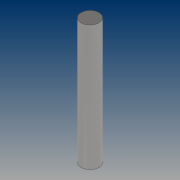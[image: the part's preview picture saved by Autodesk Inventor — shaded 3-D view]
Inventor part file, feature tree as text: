
AUTODESK INVENTOR PART (.ipt)
format: ipt  version: 2021 (Build 250183000, 183)  size: 74,752 bytes
history: native  units: mm
features: extrude x1, sketch x1
ambient origin geometry x8: Origin, YZ Plane, XZ Plane, XY Plane, X Axis, Y Axis, Z Axis, Center Point
bodies: Solid1 (feature_tree)
feature tree (2):
  extrude  "Extrusion1"  Depth=70.0mm TaperAngle=0.0deg
  sketch  "Sketch1"  dims[d0=10.0mm d1=70.0mm d2=0.0mm]
